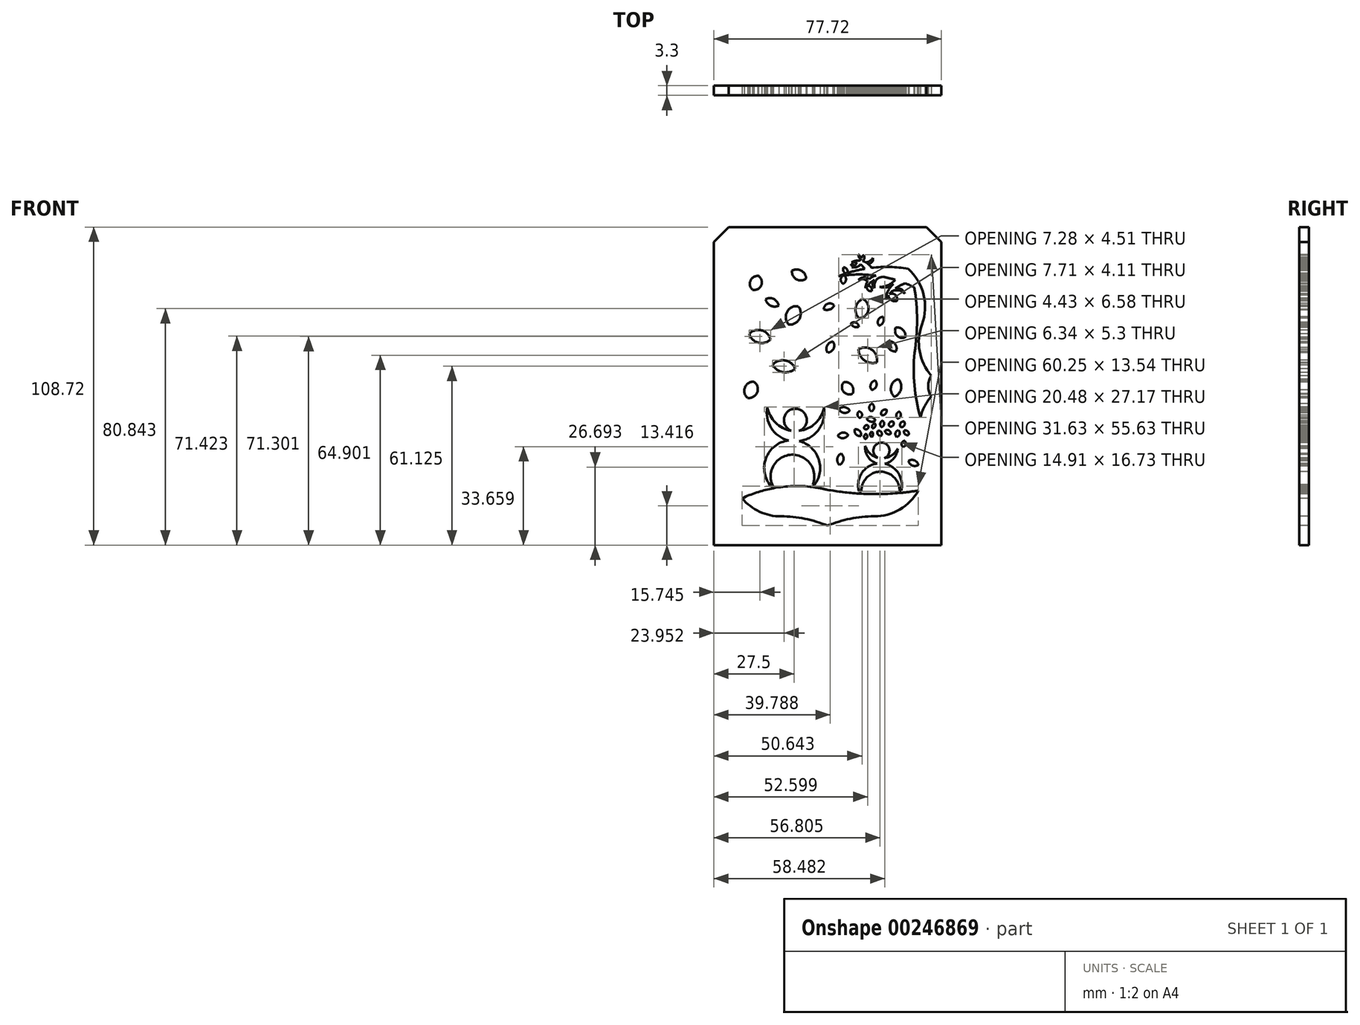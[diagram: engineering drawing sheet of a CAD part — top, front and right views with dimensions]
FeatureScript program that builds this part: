
annotation { "Feature Type Name" : "Feature", "Feature Type Description" : "" }
export const myFeature = defineFeature(function(context is Context, id is Id, definition is map)
    precondition{}
    {
        {
            var Q0;
            Q0=qCreatedBy(makeId("Front.planeOp"),FACE);
            var sketch = newSketch(context, id + "F0", { "sketchPlane" : qUnion([Q0])});
            skLineSegment(sketch, "E0.bottom", {"start": v(38.86, 54.36) * mm, "end": v(-38.86, 54.36) * mm});
            skLineSegment(sketch, "E0.top", {"start": v(38.86, -54.36) * mm, "end": v(-38.86, -54.36) * mm});
            skLineSegment(sketch, "E0.left", {"start": v(38.86, 54.36) * mm, "end": v(38.86, -54.36) * mm});
            skLineSegment(sketch, "E0.right", {"start": v(-38.86, 54.36) * mm, "end": v(-38.86, -54.36) * mm});
            skPoint(sketch, "E0.middle", {"position": v(0, 0) * mm});
            skSolve(sketch);
        }
        {
            var Q0;
            Q0=qSketchRegion(id+"F0",true);
            extrude(context, id + "F1", {"entities" : qUnion([Q0]), "depth" : 3.3 * mm});
        }
        {
            var Q0;
            Q0=makeQuery(id+"F1.opExtrude","CAP_FACE",FACE,{"disambiguationData":[OSD([sQuery(id+"F0.wireOp",EDGE,"E0.bottom"),sQuery(id+"F0.wireOp",EDGE,"E0.top"),sQuery(id+"F0.wireOp",EDGE,"E0.left"),sQuery(id+"F0.wireOp",EDGE,"E0.right")])],"isStart":false});
            var sketch = newSketch(context, id + "F2", { "sketchPlane" : qUnion([Q0])});
            skLineSegment(sketch, "E1", {"start": v(0, 57.24) * mm, "end": v(0, -57.24) * mm, "construction": true});
            skLineSegment(sketch, "E2", {"start": v(-50.8, 0) * mm, "end": v(50.8, 0) * mm, "construction": true});
            skArc(sketch, "E3", {"start": v(35.44, -3.57) * mm, "mid": v(31.46, -11.87) * mm, "end": v(32.26, -21.03) * mm});
            skLineSegment(sketch, "E4", {"start": v(15.88, -44.54) * mm, "end": v(0, -44.54) * mm, "construction": true});
            skArc(sketch, "E5", {"start": v(15.88, -44.54) * mm, "mid": v(30.2, -37.06) * mm, "end": v(32.26, -21.03) * mm});
            skArc(sketch, "E6", {"start": v(15.88, -44.54) * mm, "mid": v(7.78, -45.34) * mm, "end": v(0, -47.71) * mm});
            skArc(sketch, "E7.MirrorCS", {"start": v(-15.87, -44.54) * mm, "mid": v(-7.78, -45.34) * mm, "end": v(0, -47.71) * mm});
            skArc(sketch, "E8.MirrorCS", {"start": v(-15.87, -44.54) * mm, "mid": v(-30.2, -37.06) * mm, "end": v(-32.26, -21.03) * mm});
            skArc(sketch, "E9.MirrorCS", {"start": v(-35.44, -3.57) * mm, "mid": v(-31.46, -11.87) * mm, "end": v(-32.26, -21.03) * mm});
            skArc(sketch, "E10.MirrorCS", {"start": v(-35.44, 3.57) * mm, "mid": v(-31.46, 11.87) * mm, "end": v(-32.26, 21.03) * mm});
            skArc(sketch, "E11.MirrorCS", {"start": v(-15.88, 44.54) * mm, "mid": v(-30.2, 37.06) * mm, "end": v(-32.26, 21.03) * mm});
            skArc(sketch, "E12.MirrorCS", {"start": v(-15.88, 44.54) * mm, "mid": v(-7.78, 45.34) * mm, "end": v(0, 47.71) * mm});
            skArc(sketch, "E13.MirrorCS", {"start": v(15.87, 44.54) * mm, "mid": v(7.78, 45.34) * mm, "end": v(0, 47.71) * mm});
            skArc(sketch, "E14.MirrorCS", {"start": v(15.87, 44.54) * mm, "mid": v(30.2, 37.06) * mm, "end": v(32.26, 21.03) * mm});
            skArc(sketch, "E15.MirrorCS", {"start": v(35.44, 3.57) * mm, "mid": v(31.46, 11.87) * mm, "end": v(32.26, 21.03) * mm});
            skArc(sketch, "E16", {"start": v(35.44, 3.57) * mm, "mid": v(34.41, 0) * mm, "end": v(35.44, -3.57) * mm});
            skPoint(sketch, "E17.orphan", {"position": v(39.69, 0) * mm});
            skArc(sketch, "E18.MirrorCS", {"start": v(-35.44, 3.57) * mm, "mid": v(-34.41, 0) * mm, "end": v(-35.44, -3.57) * mm});
            skPoint(sketch, "E19.orphan", {"position": v(-39.69, 0) * mm});
            skSolve(sketch);
        }
        {
            var Q0;
            Q0=makeQuery(id+"F1.opExtrude","SWEPT_EDGE",EDGE,{"disambiguationData":[OSD([sQuery(id+"F0.wireOp",EDGE,"E0.bottom"),sQuery(id+"F0.wireOp",EDGE,"E0.right")])]});
            var Q1;
            Q1=makeQuery(id+"F1.opExtrude","SWEPT_EDGE",EDGE,{"disambiguationData":[OSD([sQuery(id+"F0.wireOp",EDGE,"E0.bottom"),sQuery(id+"F0.wireOp",EDGE,"E0.left")])]});
            chamfer(context, id + "F3", {"entities" : qUnion([Q0, Q1]), "width" : 5.08 * mm, "tangentPropagation" : true});
        }
        {
            var Q0;
            Q0=makeQuery(id+"F2.imprint","IMPRINT",FACE,{"disambiguationData":[TD([[makeQuery(id+"F2.imprint","IMPRINT",EDGE,{"derivedFrom":sQuery(id+"F2.wireOp",EDGE,"E3")}),-1.0]])]});
            var sketch = newSketch(context, id + "F4", { "sketchPlane" : qUnion([Q0])});
            skArc(sketch, "E20", {"start": v(0, -34.67) * mm, "mid": v(-2.23, -34.19) * mm, "end": v(-4.5, -33.82) * mm, "construction": true});
            skArc(sketch, "E21", {"start": v(0, -34.67) * mm, "mid": v(5.37, -35.5) * mm, "end": v(10.78, -35.99) * mm, "construction": true});
            skArc(sketch, "E22", {"start": v(-4.5, -33.82) * mm, "mid": v(-3.06, -24.92) * mm, "end": v(-9.67, -18.8) * mm});
            skArc(sketch, "E23", {"start": v(-20.56, -7.11) * mm, "mid": v(-19.26, -14.28) * mm, "end": v(-13.38, -18.57) * mm});
            skArc(sketch, "E24", {"start": v(-20.56, -7.11) * mm, "mid": v(-17.8, -12.53) * mm, "end": v(-12.38, -15.28) * mm});
            skArc(sketch, "E25", {"start": v(-5.07, -33.74) * mm, "mid": v(-12.2, -23.45) * mm, "end": v(-18.68, -34.16) * mm});
            skArc(sketch, "E26.trimOffspring", {"start": v(-9.67, -18.8) * mm, "mid": v(-3.03, -14.89) * mm, "end": v(-1.26, -7.38) * mm});
            skArc(sketch, "E27.trimOffspring", {"start": v(-13.38, -18.57) * mm, "mid": v(-21.03, -24.66) * mm, "end": v(-19.31, -34.29) * mm});
            skArc(sketch, "E28", {"start": v(-9.72, -15.32) * mm, "mid": v(-10.92, -7.74) * mm, "end": v(-12.38, -15.28) * mm});
            skArc(sketch, "E29.trimOffspring", {"start": v(-9.72, -15.32) * mm, "mid": v(-4.19, -12.74) * mm, "end": v(-1.26, -7.38) * mm});
            skArc(sketch, "E30", {"start": v(25.17, -35.72) * mm, "mid": v(24.3, -29.93) * mm, "end": v(19.52, -26.55) * mm});
            skArc(sketch, "E31", {"start": v(24.63, -35.77) * mm, "mid": v(17.98, -29.27) * mm, "end": v(11.6, -36.03) * mm});
            skArc(sketch, "E32", {"start": v(12.9, -20.48) * mm, "mid": v(13.8, -24.2) * mm, "end": v(16.9, -26.45) * mm});
            skArc(sketch, "E33", {"start": v(12.9, -20.48) * mm, "mid": v(14.5, -23.03) * mm, "end": v(17.14, -24.49) * mm});
            skArc(sketch, "E34", {"start": v(19.4, -24.62) * mm, "mid": v(18.58, -19.3) * mm, "end": v(17.14, -24.49) * mm});
            skArc(sketch, "E35.trimOffspring", {"start": v(19.4, -24.62) * mm, "mid": v(22.07, -23.57) * mm, "end": v(23.95, -21.4) * mm});
            skArc(sketch, "E36.trimOffspring", {"start": v(19.52, -26.55) * mm, "mid": v(22.63, -24.71) * mm, "end": v(23.95, -21.35) * mm});
            skArc(sketch, "E37.trimOffspring", {"start": v(16.9, -26.45) * mm, "mid": v(11.65, -29.82) * mm, "end": v(10.78, -35.99) * mm});
            skArc(sketch, "E38.0", {"start": v(15.88, -44.54) * mm, "mid": v(24.66, -42.17) * mm, "end": v(31.06, -35.7) * mm});
            skArc(sketch, "E39.0", {"start": v(15.88, -44.54) * mm, "mid": v(7.78, -45.34) * mm, "end": v(0, -47.71) * mm});
            skArc(sketch, "E40.0", {"start": v(-15.87, -44.54) * mm, "mid": v(-7.78, -45.34) * mm, "end": v(0, -47.71) * mm});
            skArc(sketch, "E41.0", {"start": v(-15.87, -44.54) * mm, "mid": v(-23.22, -42.92) * mm, "end": v(-29.2, -38.37) * mm});
            skPoint(sketch, "E42.orphan", {"position": v(32.26, -21.03) * mm});
            skPoint(sketch, "E43.orphan", {"position": v(32.57, -34.67) * mm});
            skArc(sketch, "E44.trimOffspring", {"start": v(25.17, -35.72) * mm, "mid": v(28.35, -35.34) * mm, "end": v(31.5, -34.86) * mm, "construction": true});
            skArc(sketch, "E45.trimOffspring", {"start": v(11.6, -36.03) * mm, "mid": v(18.12, -36.14) * mm, "end": v(24.63, -35.77) * mm, "construction": true});
            skArc(sketch, "E46.trimOffspring", {"start": v(-5.07, -33.74) * mm, "mid": v(-11.89, -33.43) * mm, "end": v(-18.68, -34.16) * mm, "construction": true});
            skArc(sketch, "E47.trimOffspring", {"start": v(-19.31, -34.29) * mm, "mid": v(-24.6, -35.7) * mm, "end": v(-29.7, -37.76) * mm, "construction": true});
            skPoint(sketch, "E48.orphan", {"position": v(-32.26, -21.03) * mm});
            skArc(sketch, "E49.0", {"start": v(-19.16, -35.04) * mm, "mid": v(-24.28, -36.4) * mm, "end": v(-29.2, -38.37) * mm});
            skArc(sketch, "E50.0", {"start": v(-5.16, -34.5) * mm, "mid": v(-11.87, -34.2) * mm, "end": v(-18.54, -34.91) * mm});
            skArc(sketch, "E51.0", {"start": v(-0.16, -35.42) * mm, "mid": v(5.27, -36.25) * mm, "end": v(10.73, -36.75) * mm});
            skArc(sketch, "E51.1", {"start": v(-0.16, -35.42) * mm, "mid": v(-2.37, -34.94) * mm, "end": v(-4.6, -34.57) * mm});
            skArc(sketch, "E52.0", {"start": v(11.55, -36.8) * mm, "mid": v(18.13, -36.9) * mm, "end": v(24.7, -36.53) * mm});
            skArc(sketch, "E53.0", {"start": v(25.25, -36.47) * mm, "mid": v(28.16, -36.14) * mm, "end": v(31.06, -35.7) * mm});
            skArc(sketch, "E54", {"start": v(-18.68, -34.16) * mm, "mid": v(-19, -34.2) * mm, "end": v(-19.31, -34.29) * mm});
            skArc(sketch, "E55", {"start": v(-18.54, -34.91) * mm, "mid": v(-18.85, -34.97) * mm, "end": v(-19.16, -35.04) * mm});
            skArc(sketch, "E56", {"start": v(-4.5, -33.82) * mm, "mid": v(-4.78, -33.77) * mm, "end": v(-5.07, -33.74) * mm});
            skArc(sketch, "E57", {"start": v(-4.6, -34.57) * mm, "mid": v(-4.88, -34.53) * mm, "end": v(-5.16, -34.5) * mm});
            skArc(sketch, "E58", {"start": v(10.78, -35.99) * mm, "mid": v(11.19, -36.02) * mm, "end": v(11.6, -36.03) * mm});
            skArc(sketch, "E59", {"start": v(10.73, -36.75) * mm, "mid": v(11.14, -36.78) * mm, "end": v(11.55, -36.8) * mm});
            skArc(sketch, "E60", {"start": v(25.17, -35.72) * mm, "mid": v(24.9, -35.73) * mm, "end": v(24.63, -35.77) * mm});
            skArc(sketch, "E61", {"start": v(24.7, -36.53) * mm, "mid": v(24.98, -36.51) * mm, "end": v(25.25, -36.47) * mm});
            skArc(sketch, "E62", {"start": v(9.31, -14.83) * mm, "mid": v(9.72, -16.53) * mm, "end": v(11.4, -17.02) * mm});
            skArc(sketch, "E63", {"start": v(11.4, -17.02) * mm, "mid": v(10.98, -15.33) * mm, "end": v(9.31, -14.83) * mm});
            skArc(sketch, "E64", {"start": v(13.1, -16.34) * mm, "mid": v(12.5, -17.16) * mm, "end": v(12.85, -18.1) * mm});
            skArc(sketch, "E65", {"start": v(12.85, -18.1) * mm, "mid": v(13.57, -17.3) * mm, "end": v(13.1, -16.34) * mm});
            skArc(sketch, "E66", {"start": v(13.97, -13.6) * mm, "mid": v(12.91, -13.52) * mm, "end": v(12.53, -14.5) * mm});
            skArc(sketch, "E67", {"start": v(12.53, -14.5) * mm, "mid": v(13.62, -14.64) * mm, "end": v(13.97, -13.6) * mm});
            skArc(sketch, "E68", {"start": v(15.15, -15.56) * mm, "mid": v(14.54, -16.49) * mm, "end": v(15.15, -17.42) * mm});
            skArc(sketch, "E69", {"start": v(15.15, -17.42) * mm, "mid": v(15.56, -16.49) * mm, "end": v(15.15, -15.56) * mm});
            skArc(sketch, "E70", {"start": v(16.18, -12.77) * mm, "mid": v(15.34, -13.4) * mm, "end": v(15.34, -14.43) * mm});
            skArc(sketch, "E71", {"start": v(15.34, -14.43) * mm, "mid": v(16.27, -13.86) * mm, "end": v(16.18, -12.77) * mm});
            skArc(sketch, "E72", {"start": v(17.21, -15.25) * mm, "mid": v(17.2, -16.5) * mm, "end": v(18.32, -17.04) * mm});
            skArc(sketch, "E73", {"start": v(18.32, -17.04) * mm, "mid": v(18.4, -15.75) * mm, "end": v(17.21, -15.25) * mm});
            skArc(sketch, "E74", {"start": v(18.76, -11.85) * mm, "mid": v(17.98, -12.83) * mm, "end": v(18.47, -14) * mm});
            skArc(sketch, "E75", {"start": v(18.47, -14) * mm, "mid": v(19.35, -13.02) * mm, "end": v(18.76, -11.85) * mm});
            skArc(sketch, "E76", {"start": v(19.61, -15.28) * mm, "mid": v(20.33, -16.34) * mm, "end": v(21.6, -16.34) * mm});
            skArc(sketch, "E77", {"start": v(21.6, -16.34) * mm, "mid": v(20.96, -15.14) * mm, "end": v(19.61, -15.28) * mm});
            skArc(sketch, "E78", {"start": v(22.38, -12.13) * mm, "mid": v(21.21, -12.5) * mm, "end": v(21.1, -13.71) * mm});
            skArc(sketch, "E79", {"start": v(21.1, -13.71) * mm, "mid": v(22.4, -13.45) * mm, "end": v(22.38, -12.13) * mm});
            skArc(sketch, "E80", {"start": v(13.42, -11.15) * mm, "mid": v(14.72, -12.15) * mm, "end": v(16.34, -11.85) * mm});
            skArc(sketch, "E81", {"start": v(16.34, -11.85) * mm, "mid": v(15.08, -10.63) * mm, "end": v(13.42, -11.15) * mm});
            skArc(sketch, "E82", {"start": v(20.13, -8.06) * mm, "mid": v(18.68, -8.46) * mm, "end": v(18.42, -9.94) * mm});
            skArc(sketch, "E83", {"start": v(18.42, -9.94) * mm, "mid": v(19.81, -9.49) * mm, "end": v(20.13, -8.06) * mm});
            skArc(sketch, "E84", {"start": v(24.26, -15.08) * mm, "mid": v(23.2, -16.04) * mm, "end": v(23.64, -17.39) * mm});
            skArc(sketch, "E85", {"start": v(23.64, -17.39) * mm, "mid": v(24.65, -16.42) * mm, "end": v(24.26, -15.08) * mm});
            skArc(sketch, "E86", {"start": v(24.49, -8.74) * mm, "mid": v(23.52, -9.78) * mm, "end": v(24, -11.12) * mm});
            skArc(sketch, "E87", {"start": v(24, -11.12) * mm, "mid": v(25.02, -10.09) * mm, "end": v(24.49, -8.74) * mm});
            skArc(sketch, "E88", {"start": v(26.15, -12.14) * mm, "mid": v(24.92, -12.7) * mm, "end": v(25.03, -14.04) * mm});
            skArc(sketch, "E89", {"start": v(25.03, -14.04) * mm, "mid": v(26.22, -13.46) * mm, "end": v(26.15, -12.14) * mm});
            skArc(sketch, "E90", {"start": v(26.15, -15.24) * mm, "mid": v(26.48, -16.45) * mm, "end": v(27.7, -16.7) * mm});
            skArc(sketch, "E91", {"start": v(27.7, -16.7) * mm, "mid": v(27.42, -15.46) * mm, "end": v(26.15, -15.24) * mm});
            skArc(sketch, "E92", {"start": v(26.38, -18.76) * mm, "mid": v(25.28, -19.6) * mm, "end": v(25.92, -20.81) * mm});
            skArc(sketch, "E93", {"start": v(25.92, -20.81) * mm, "mid": v(26.73, -19.91) * mm, "end": v(26.38, -18.76) * mm});
            skArc(sketch, "E94", {"start": v(10.79, -8.68) * mm, "mid": v(10.24, -9.87) * mm, "end": v(11.06, -10.89) * mm});
            skArc(sketch, "E95", {"start": v(11.06, -10.89) * mm, "mid": v(11.78, -9.68) * mm, "end": v(10.79, -8.68) * mm});
            skArc(sketch, "E96", {"start": v(15.2, -6.01) * mm, "mid": v(14.25, -7.26) * mm, "end": v(14.97, -8.66) * mm});
            skArc(sketch, "E97", {"start": v(14.97, -8.66) * mm, "mid": v(15.89, -7.4) * mm, "end": v(15.2, -6.01) * mm});
            skArc(sketch, "E98", {"start": v(4.67, -23.04) * mm, "mid": v(3.33, -24.81) * mm, "end": v(4.05, -26.91) * mm});
            skArc(sketch, "E99", {"start": v(4.05, -26.91) * mm, "mid": v(5.45, -25.15) * mm, "end": v(4.67, -23.04) * mm});
            skArc(sketch, "E100", {"start": v(3.56, -17.06) * mm, "mid": v(5.38, -17.8) * mm, "end": v(7.02, -16.72) * mm});
            skArc(sketch, "E101", {"start": v(7.02, -16.72) * mm, "mid": v(5.2, -15.89) * mm, "end": v(3.56, -17.06) * mm});
            skArc(sketch, "E102", {"start": v(27.63, -25.6) * mm, "mid": v(28.98, -27.16) * mm, "end": v(31.03, -26.97) * mm});
            skArc(sketch, "E103", {"start": v(31.03, -26.97) * mm, "mid": v(29.7, -25.4) * mm, "end": v(27.63, -25.6) * mm});
            skArc(sketch, "E104", {"start": v(-10.03, 27.29) * mm, "mid": v(-13.88, 25.27) * mm, "end": v(-13.19, 20.98) * mm});
            skArc(sketch, "E105", {"start": v(-13.19, 20.98) * mm, "mid": v(-9.55, 23.1) * mm, "end": v(-10.03, 27.29) * mm});
            skArc(sketch, "E106", {"start": v(10.57, 12.56) * mm, "mid": v(12.59, 8.79) * mm, "end": v(16.81, 8.09) * mm});
            skArc(sketch, "E107", {"start": v(16.81, 8.09) * mm, "mid": v(15.18, 12.41) * mm, "end": v(10.57, 12.56) * mm});
            skArc(sketch, "E108", {"start": v(12.09, 29.77) * mm, "mid": v(9.63, 26.83) * mm, "end": v(10.82, 23.2) * mm});
            skArc(sketch, "E109", {"start": v(10.82, 23.2) * mm, "mid": v(13.97, 26) * mm, "end": v(12.09, 29.77) * mm});
            skArc(sketch, "E110", {"start": v(-18.76, 7.23) * mm, "mid": v(-15.2, 4.77) * mm, "end": v(-11.05, 5.97) * mm});
            skArc(sketch, "E111", {"start": v(-11.05, 5.97) * mm, "mid": v(-14.55, 8.78) * mm, "end": v(-18.76, 7.23) * mm});
            skArc(sketch, "E112", {"start": v(1.84, 15.18) * mm, "mid": v(-0.13, 13.83) * mm, "end": v(0, 11.45) * mm});
            skArc(sketch, "E113", {"start": v(0, 11.45) * mm, "mid": v(2.05, 12.76) * mm, "end": v(1.84, 15.18) * mm});
            skArc(sketch, "E114", {"start": v(29.65, 33.75) * mm, "mid": v(28.14, 34.46) * mm, "end": v(26.6, 35.1) * mm});
            skArc(sketch, "E115", {"start": v(27.54, 40.08) * mm, "mid": v(21.3, 40.7) * mm, "end": v(15.02, 40.41) * mm});
            skArc(sketch, "E116", {"start": v(16.54, 37.76) * mm, "mid": v(15.31, 37.3) * mm, "end": v(14.27, 36.53) * mm});
            skArc(sketch, "E117", {"start": v(18.93, 37.36) * mm, "mid": v(18.03, 37.15) * mm, "end": v(17.15, 36.84) * mm});
            skArc(sketch, "E118", {"start": v(22.53, 34.92) * mm, "mid": v(20.67, 32.5) * mm, "end": v(19.83, 29.6) * mm});
            skArc(sketch, "E119", {"start": v(26.6, 35.1) * mm, "mid": v(24.8, 34.38) * mm, "end": v(23.15, 33.37) * mm});
            skArc(sketch, "E120", {"start": v(17.75, 33.92) * mm, "mid": v(20.27, 33.79) * mm, "end": v(22.53, 34.92) * mm});
            skArc(sketch, "E121", {"start": v(17.75, 33.92) * mm, "mid": v(20.71, 34.48) * mm, "end": v(23.08, 36.34) * mm});
            skArc(sketch, "E122.trimOffspring", {"start": v(23.08, 36.34) * mm, "mid": v(21.02, 36.9) * mm, "end": v(18.93, 37.36) * mm});
            skArc(sketch, "E123", {"start": v(26.43, 31.55) * mm, "mid": v(25.14, 33.08) * mm, "end": v(23.15, 33.37) * mm});
            skArc(sketch, "E124", {"start": v(26.43, 31.55) * mm, "mid": v(24.3, 32.73) * mm, "end": v(21.9, 32.31) * mm});
            skArc(sketch, "E125", {"start": v(15.97, 36.26) * mm, "mid": v(15.39, 34.89) * mm, "end": v(16, 33.53) * mm});
            skArc(sketch, "E126", {"start": v(17.15, 36.84) * mm, "mid": v(16.18, 35.33) * mm, "end": v(16, 33.53) * mm});
            skArc(sketch, "E127", {"start": v(14.27, 36.53) * mm, "mid": v(12.35, 37.16) * mm, "end": v(10.55, 36.25) * mm});
            skArc(sketch, "E128", {"start": v(13.7, 35.83) * mm, "mid": v(12.2, 36.53) * mm, "end": v(10.55, 36.25) * mm});
            skArc(sketch, "E129", {"start": v(12.68, 40.07) * mm, "mid": v(12.05, 40.9) * mm, "end": v(11.24, 41.58) * mm});
            skArc(sketch, "E130", {"start": v(15.02, 40.41) * mm, "mid": v(14.4, 41.25) * mm, "end": v(13.63, 41.95) * mm});
            skArc(sketch, "E131", {"start": v(13.63, 41.95) * mm, "mid": v(15.11, 42.29) * mm, "end": v(15.47, 43.77) * mm});
            skArc(sketch, "E132", {"start": v(13.1, 42.29) * mm, "mid": v(14.46, 42.75) * mm, "end": v(15.47, 43.77) * mm});
            skPoint(sketch, "E132.startSnap0", {"position": v(15.11, 42.29) * mm});
            skArc(sketch, "E133", {"start": v(12, 42.74) * mm, "mid": v(12.6, 43.62) * mm, "end": v(12.45, 44.68) * mm});
            skPoint(sketch, "E133.endSnap0", {"position": v(12, 42.74) * mm});
            skArc(sketch, "E134", {"start": v(10.9, 42.92) * mm, "mid": v(11.2, 43.11) * mm, "end": v(11.46, 43.36) * mm});
            skArc(sketch, "E135", {"start": v(10.78, 44.86) * mm, "mid": v(11.21, 44.3) * mm, "end": v(11.86, 44) * mm});
            skArc(sketch, "E136", {"start": v(10.6, 44.88) * mm, "mid": v(10.79, 43.98) * mm, "end": v(11.46, 43.36) * mm});
            skArc(sketch, "E137", {"start": v(8.26, 40.6) * mm, "mid": v(8.65, 40.73) * mm, "end": v(9.02, 40.92) * mm});
            skArc(sketch, "E138", {"start": v(8.26, 40.6) * mm, "mid": v(9.88, 40.69) * mm, "end": v(11.24, 41.58) * mm});
            skArc(sketch, "E139", {"start": v(9.32, 41.15) * mm, "mid": v(8.63, 41.55) * mm, "end": v(7.86, 41.36) * mm});
            skArc(sketch, "E140", {"start": v(9.02, 40.92) * mm, "mid": v(8.5, 41.3) * mm, "end": v(7.86, 41.36) * mm});
            skArc(sketch, "E141", {"start": v(5.47, 37.81) * mm, "mid": v(4.51, 36.43) * mm, "end": v(5.38, 34.99) * mm});
            skArc(sketch, "E142", {"start": v(5.38, 34.99) * mm, "mid": v(6.3, 36.32) * mm, "end": v(5.73, 37.84) * mm});
            skArc(sketch, "E143", {"start": v(20.78, 31.05) * mm, "mid": v(21.77, 29.37) * mm, "end": v(23.7, 29.11) * mm});
            skArc(sketch, "E144", {"start": v(23.7, 29.11) * mm, "mid": v(23.18, 31.13) * mm, "end": v(21.13, 31.48) * mm});
            skArc(sketch, "E145", {"start": v(13.38, 34.02) * mm, "mid": v(13.83, 32.82) * mm, "end": v(15.05, 32.42) * mm});
            skArc(sketch, "E146", {"start": v(15.05, 32.42) * mm, "mid": v(14.86, 33.8) * mm, "end": v(13.52, 34.2) * mm});
            skArc(sketch, "E147", {"start": v(5.47, 40.56) * mm, "mid": v(5.42, 39.3) * mm, "end": v(6.43, 38.52) * mm});
            skArc(sketch, "E148", {"start": v(6.7, 38.61) * mm, "mid": v(6.65, 39.94) * mm, "end": v(5.47, 40.56) * mm});
            skArc(sketch, "E149.trimOffspring", {"start": v(6.43, 38.52) * mm, "mid": v(5.1, 38.07) * mm, "end": v(3.8, 37.57) * mm});
            skArc(sketch, "E150.trimOffspring", {"start": v(5.47, 37.81) * mm, "mid": v(4.64, 37.7) * mm, "end": v(3.8, 37.57) * mm});
            skArc(sketch, "E151.0", {"start": v(12.45, 44.68) * mm, "mid": v(12.24, 44.7) * mm, "end": v(12.02, 44.72) * mm});
            skPoint(sketch, "E152.orphan", {"position": v(12, 45.19) * mm});
            skArc(sketch, "E153.trimOffspring", {"start": v(10.78, 44.86) * mm, "mid": v(10.7, 44.87) * mm, "end": v(10.6, 44.88) * mm});
            skPoint(sketch, "E154.orphan", {"position": v(0, 47.71) * mm});
            skArc(sketch, "E155.trimOffspring", {"start": v(11.86, 44) * mm, "mid": v(11.97, 44.35) * mm, "end": v(12.02, 44.72) * mm});
            skArc(sketch, "E156.trimOffspring", {"start": v(10.9, 42.92) * mm, "mid": v(9.5, 42.8) * mm, "end": v(8.2, 42.32) * mm});
            skPoint(sketch, "E157.orphan", {"position": v(15.87, 44.54) * mm});
            skArc(sketch, "E158.trimOffspring", {"start": v(13.1, 42.29) * mm, "mid": v(12.56, 42.54) * mm, "end": v(12, 42.74) * mm});
            skArc(sketch, "E159.trimOffspring", {"start": v(12.68, 40.07) * mm, "mid": v(9.67, 39.45) * mm, "end": v(6.7, 38.61) * mm});
            skArc(sketch, "E160.trimOffspring", {"start": v(9.96, 42.17) * mm, "mid": v(9.09, 42.33) * mm, "end": v(8.2, 42.32) * mm});
            skArc(sketch, "E161.trimOffspring", {"start": v(9.32, 41.15) * mm, "mid": v(9.7, 41.62) * mm, "end": v(9.96, 42.17) * mm});
            skArc(sketch, "E162.trimOffspring", {"start": v(13.7, 35.83) * mm, "mid": v(13.17, 34.69) * mm, "end": v(12.96, 33.45) * mm});
            skArc(sketch, "E163.trimOffspring", {"start": v(15.97, 36.26) * mm, "mid": v(14.66, 35.33) * mm, "end": v(13.52, 34.2) * mm});
            skArc(sketch, "E164.trimOffspring", {"start": v(16.54, 37.76) * mm, "mid": v(11.14, 38.15) * mm, "end": v(5.73, 37.84) * mm});
            skArc(sketch, "E165.trimOffspring", {"start": v(13.38, 34.02) * mm, "mid": v(13.16, 33.74) * mm, "end": v(12.96, 33.45) * mm});
            skArc(sketch, "E166.trimOffspring", {"start": v(21.9, 32.31) * mm, "mid": v(21.5, 31.9) * mm, "end": v(21.13, 31.48) * mm});
            skPoint(sketch, "E167.orphan", {"position": v(32.26, 21.03) * mm});
            skArc(sketch, "E168.trimOffspring", {"start": v(20.78, 31.05) * mm, "mid": v(20.28, 30.34) * mm, "end": v(19.83, 29.6) * mm});
            skArc(sketch, "E169", {"start": v(-23.57, 37.65) * mm, "mid": v(-26.33, 36.02) * mm, "end": v(-25.59, 32.9) * mm});
            skArc(sketch, "E170", {"start": v(-25.59, 32.9) * mm, "mid": v(-22.66, 34.46) * mm, "end": v(-23.57, 37.65) * mm});
            skArc(sketch, "E171", {"start": v(-12.13, 39.44) * mm, "mid": v(-10.62, 36.47) * mm, "end": v(-7.3, 36.8) * mm});
            skArc(sketch, "E172", {"start": v(-7.3, 36.8) * mm, "mid": v(-8.98, 39.46) * mm, "end": v(-12.13, 39.44) * mm});
            skArc(sketch, "E173", {"start": v(-26.75, 17.83) * mm, "mid": v(-23.65, 14.83) * mm, "end": v(-19.48, 15.93) * mm});
            skArc(sketch, "E174", {"start": v(-19.48, 15.93) * mm, "mid": v(-22.54, 19.06) * mm, "end": v(-26.75, 17.83) * mm});
            skArc(sketch, "E175", {"start": v(-25.17, 1.48) * mm, "mid": v(-28.24, -0.54) * mm, "end": v(-27.24, -4.07) * mm});
            skArc(sketch, "E176", {"start": v(-27.24, -4.07) * mm, "mid": v(-24, -2.12) * mm, "end": v(-25.17, 1.48) * mm});
            skArc(sketch, "E177", {"start": v(23.33, 20.05) * mm, "mid": v(23.76, 17.2) * mm, "end": v(26.6, 16.69) * mm});
            skArc(sketch, "E178", {"start": v(26.6, 16.69) * mm, "mid": v(25.8, 19.18) * mm, "end": v(23.33, 20.05) * mm});
            skArc(sketch, "E179.0", {"start": v(27.54, 40.08) * mm, "mid": v(32.82, 31.28) * mm, "end": v(32.26, 21.03) * mm});
            skArc(sketch, "E180", {"start": v(29.71, 11.36) * mm, "mid": v(29.7, 0.21) * mm, "end": v(31.7, -10.75) * mm});
            skArc(sketch, "E181", {"start": v(29.71, 11.36) * mm, "mid": v(30.6, 22.55) * mm, "end": v(29.65, 33.75) * mm});
            skArc(sketch, "E182.0", {"start": v(35.44, 3.57) * mm, "mid": v(31.46, 11.87) * mm, "end": v(32.26, 21.03) * mm});
            skArc(sketch, "E183.0", {"start": v(35.44, 3.57) * mm, "mid": v(34.41, 0) * mm, "end": v(35.44, -3.57) * mm});
            skArc(sketch, "E184.0", {"start": v(35.44, -3.57) * mm, "mid": v(33.15, -6.94) * mm, "end": v(31.7, -10.75) * mm});
            skArc(sketch, "E185", {"start": v(5.55, 1.35) * mm, "mid": v(5.45, -1.9) * mm, "end": v(8.63, -2.53) * mm});
            skArc(sketch, "E186", {"start": v(8.63, -2.53) * mm, "mid": v(8.21, 0.3) * mm, "end": v(5.55, 1.35) * mm});
            skArc(sketch, "E187", {"start": v(24.16, 2.38) * mm, "mid": v(21.71, -0.23) * mm, "end": v(22.84, -3.63) * mm});
            skArc(sketch, "E188", {"start": v(22.84, -3.63) * mm, "mid": v(25.12, -0.98) * mm, "end": v(24.16, 2.38) * mm});
            skArc(sketch, "E189", {"start": v(7.53, -8.42) * mm, "mid": v(5.9, -7.2) * mm, "end": v(3.96, -7.83) * mm});
            skArc(sketch, "E190", {"start": v(3.96, -7.83) * mm, "mid": v(5.57, -9.16) * mm, "end": v(7.53, -8.42) * mm});
            skArc(sketch, "E191", {"start": v(16.25, 1.9) * mm, "mid": v(14.78, 0.62) * mm, "end": v(15.08, -1.3) * mm});
            skArc(sketch, "E192", {"start": v(15.08, -1.3) * mm, "mid": v(16.66, -0.07) * mm, "end": v(16.25, 1.9) * mm});
            skArc(sketch, "E193", {"start": v(2.3, 27.6) * mm, "mid": v(0.07, 28.14) * mm, "end": v(-1.3, 26.28) * mm});
            skArc(sketch, "E194", {"start": v(-1.3, 26.28) * mm, "mid": v(0.78, 26.2) * mm, "end": v(2.3, 27.6) * mm});
            skArc(sketch, "E195", {"start": v(10.65, 20.27) * mm, "mid": v(9.7, 21.7) * mm, "end": v(8.02, 21.42) * mm});
            skArc(sketch, "E196", {"start": v(8.02, 21.42) * mm, "mid": v(9.08, 20.26) * mm, "end": v(10.65, 20.27) * mm});
            skArc(sketch, "E197", {"start": v(20.62, 15.16) * mm, "mid": v(21.08, 12.77) * mm, "end": v(23.32, 11.84) * mm});
            skArc(sketch, "E198", {"start": v(23.32, 11.84) * mm, "mid": v(23.07, 14.4) * mm, "end": v(20.62, 15.16) * mm});
            skArc(sketch, "E199", {"start": v(18.93, 23.66) * mm, "mid": v(17.34, 22.59) * mm, "end": v(17.58, 20.68) * mm});
            skArc(sketch, "E200", {"start": v(17.58, 20.68) * mm, "mid": v(19.01, 21.83) * mm, "end": v(18.93, 23.66) * mm});
            skArc(sketch, "E201", {"start": v(-21.16, 29.72) * mm, "mid": v(-19.48, 27.48) * mm, "end": v(-16.68, 27.48) * mm});
            skArc(sketch, "E202", {"start": v(-16.68, 27.48) * mm, "mid": v(-18.35, 29.75) * mm, "end": v(-21.16, 29.72) * mm});
            skSolve(sketch);
        }
        {
            var Q0;
            Q0=qSketchRegion(id+"F4",true);
            extrude(context, id + "F5", {"entities" : qUnion([Q0]), "operationType" : NewBodyOperationType.REMOVE, "endBound" : BoundingType.THROUGH_ALL, "oppositeDirection" : true, "depth" : 25.4 * mm});
        }
    });
